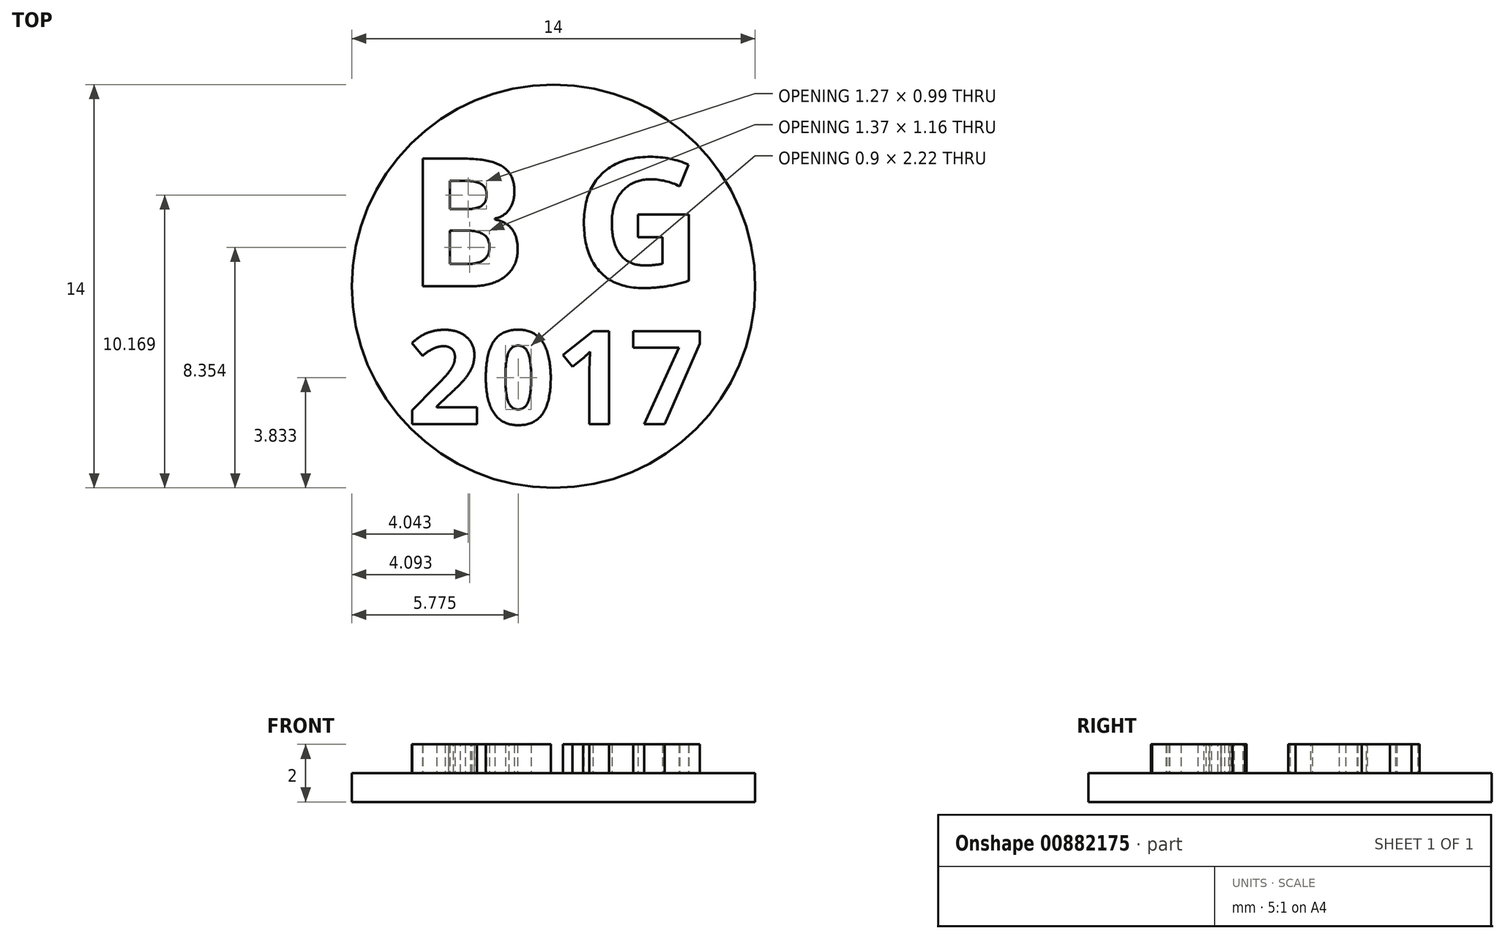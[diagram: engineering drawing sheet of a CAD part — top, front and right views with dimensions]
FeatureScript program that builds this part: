
annotation { "Feature Type Name" : "Feature", "Feature Type Description" : "" }
export const myFeature = defineFeature(function(context is Context, id is Id, definition is map)
    precondition{}
    {
        {
            var Q0;
            Q0=qCreatedBy(makeId("Top.planeOp"),FACE);
            var sketch = newSketch(context, id + "F0", { "sketchPlane" : qUnion([Q0])});
            skCircle(sketch, "E0", {"center": v(0, 0) * mm, "radius": 7 * mm});
            skSolve(sketch);
        }
        {
            var Q0;
            Q0 = qSketchRegion(id + "F0", true);
            extrude(context, id + "F1", {"entities" : qUnion([Q0]), "depth" : 1 * mm, "offsetDistance" : 25 * mm});
        }
        {
            var Q0;
            Q0=makeQuery(id+"F1.opExtrude","CAP_FACE",FACE,{"disambiguationData":[OSD([sQuery(id+"F0.wireOp",EDGE,"E0")])],"isStart":false});
            cPlane(context, id + "F2", {"entities" : qUnion([Q0]), "cplaneType" : CPlaneType.OFFSET, "offset" : 0 * mm, "width" : 150 * mm, "height" : 150 * mm});
        }
        {
            var Q0;
            Q0=qCreatedBy(id+"F2.planeOp",FACE);
            var sketch = newSketch(context, id + "F3", { "sketchPlane" : qUnion([Q0])});
            skText(sketch, "E1", { "text": "B G", "fontName": "OpenSans-Bold.ttf"});
            skText(sketch, "E2", { "text": "2017\n", "fontName": "OpenSans-Bold.ttf"});
            const initialGuessF3  = {"E1": [-0.00509, 0, 1, 0, 0.00447], "E2": [-0.00509, -0.00478, 1, 0, 0.00325]};
            skSetInitialGuess(sketch, initialGuessF3);
            skSolve(sketch);
        }
        {
            var Q0;
            Q0 = qSketchRegion(id + "F3", true);
            extrude(context, id + "F4", {"entities" : qUnion([Q0]), "depth" : 1 * mm, "offsetDistance" : 25 * mm});
        }
    });
